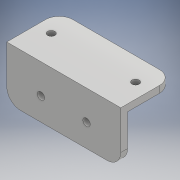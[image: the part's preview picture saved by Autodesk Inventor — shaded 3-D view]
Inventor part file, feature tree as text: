
AUTODESK INVENTOR PART (.ipt)
format: ipt  version: 2018 (Build 220112000, 112)  size: 139,776 bytes
history: native  units: mm
features: extrude x4, sketch x4, fillet x1
ambient origin geometry x8: Origin, YZ Plane, XZ Plane, XY Plane, X Axis, Y Axis, Z Axis, Center Point
bodies: Solid1 (feature_tree)
feature tree (9):
  extrude  "Extrusion1"  Depth=23.0mm
  extrude  "Extrusion2"  Depth=3.0mm
  extrude  "Extrusion3"  Depth=20.0mm
  fillet  "Fillet1"  Radius=3.2mm
  extrude  "Extrusion4"  Depth=20.0mm
  sketch  "Sketch1"  dims[d0=50.0mm d1=23.0mm]
  sketch  "Sketch2"  dims[d2=3.0mm d3=0.0mm d4=3.0mm]
  sketch  "Sketch3"  dims[d5=20.0mm d6=0.0mm d7=3.2mm d8=3.2mm]
  sketch  "Sketch4"  dims[d9=37.0mm d10=6.5mm d11=10.0mm d12=10.0mm d13=20.0mm d14=0.0mm d15=6.0mm d17=3.2mm d18=3.2mm d19=10.0mm d20=20.0mm d21=15.0mm d22=20.0mm d23=0.0mm]
